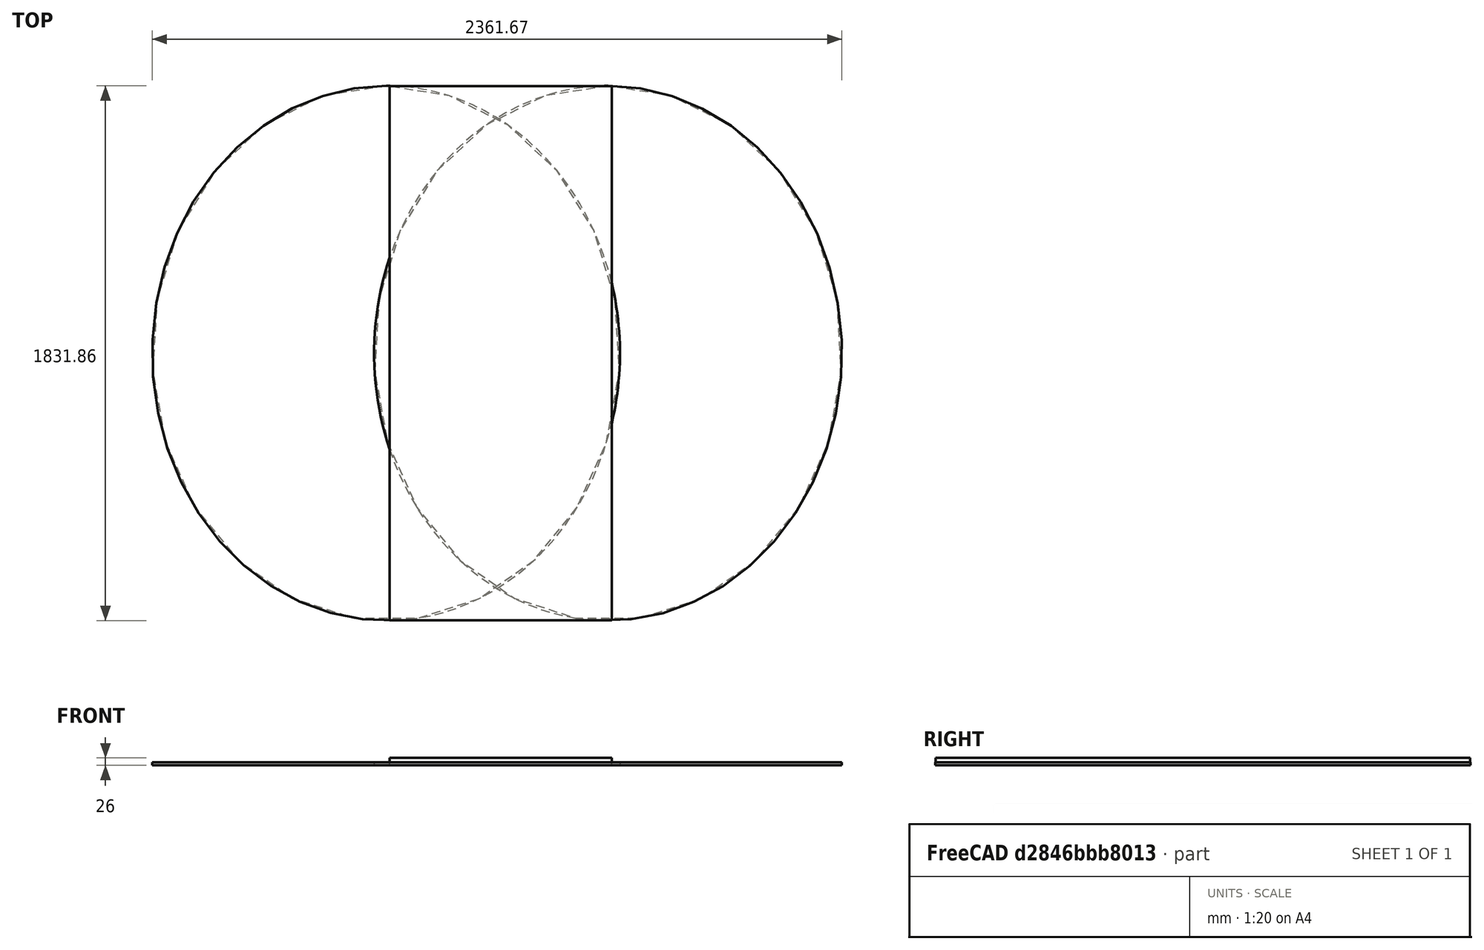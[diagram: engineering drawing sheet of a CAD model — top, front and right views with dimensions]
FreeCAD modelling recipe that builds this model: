
FCSTD DOCUMENT  (FreeCAD 0.21R33771 (Git))
Label: safety
License: All rights reserved
LicenseURL: https://en.wikipedia.org/wiki/All_rights_reserved
objects: Sketcher::SketchObject×2, Part::Extrusion×2, Part::Box×1, PartDesign::Body×1
note: 6 computed .brp shape members not serialized (recipe doc carries the construction recipe); baked Part::Feature solids carry a one-line shape summary decoded from their .brp

FEATURE [Part::Box] Box  label="Cube"
  AttacherType = Attacher::AttachEngine3D
  Height = 26
  Length = 760
  Width = 1830
  expr: Length = 760 mm
FEATURE [Sketcher::SketchObject] Sketch
  FullyConstrained = false
  MapMode = 5
  Support = -> [XY_Plane]
  sketch-geometry (5):
    g0: Ellipse CenterX=747.518 CenterY=915.251 CenterZ=0 NormalX=0 NormalY=0 NormalZ=1 MajorRadius=915.934 MinorRadius=800.836 AngleXU=1.56982
    g1: LineSegment StartX=748.413 StartY=1831.18 StartZ=0 EndX=746.623 EndY=-0.682911 EndZ=0
    g2: LineSegment StartX=-53.3171 StartY=916.034 StartZ=0 EndX=1548.35 EndY=914.468 EndZ=0
    g3: GeomPoint X=747.953 Y=1359.77 Z=0
    g4: GeomPoint X=747.084 Y=470.731 Z=0
  constraints (1):
    c: InternalAlignment(g1-g4 -> g0) x4
FEATURE [PartDesign::Body] Body
  Group = -> [Sketch]
  Origin = -> Origin
FEATURE [Part::Extrusion] Extrude
  Base = -> Sketch
  Dir = (0,0,1)
  DirMode = 0
  FaceMakerClass = Part::FaceMakerBullseye
  LengthFwd = 10
  LengthRev = 0
  Solid = true
  Symmetric = false
FEATURE [Sketcher::SketchObject] Sketch001
  FullyConstrained = false
  MapMode = 5
  Support = -> [XY_Plane001]
  sketch-geometry (5):
    g0: Ellipse CenterX=747.518 CenterY=915.251 CenterZ=0 NormalX=0 NormalY=0 NormalZ=1 MajorRadius=915.934 MinorRadius=800.836 AngleXU=1.56982
    g1: LineSegment StartX=748.413 StartY=1831.18 StartZ=0 EndX=746.623 EndY=-0.682911 EndZ=0
    g2: LineSegment StartX=-53.3171 StartY=916.034 StartZ=0 EndX=1548.35 EndY=914.468 EndZ=0
    g3: GeomPoint X=747.953 Y=1359.77 Z=0
    g4: GeomPoint X=747.084 Y=470.731 Z=0
  constraints (1):
    c: InternalAlignment(g1-g4 -> g0) x4
FEATURE [Part::Extrusion] Extrude001
  Base = -> Sketch001
  Dir = (0,0,1)
  DirMode = 0
  FaceMakerClass = Part::FaceMakerBullseye
  LengthFwd = 10
  LengthRev = 0
  Placement = pos=(-760,0,0) rot=(0,0,1;0rad)
  Solid = true
  Symmetric = false
